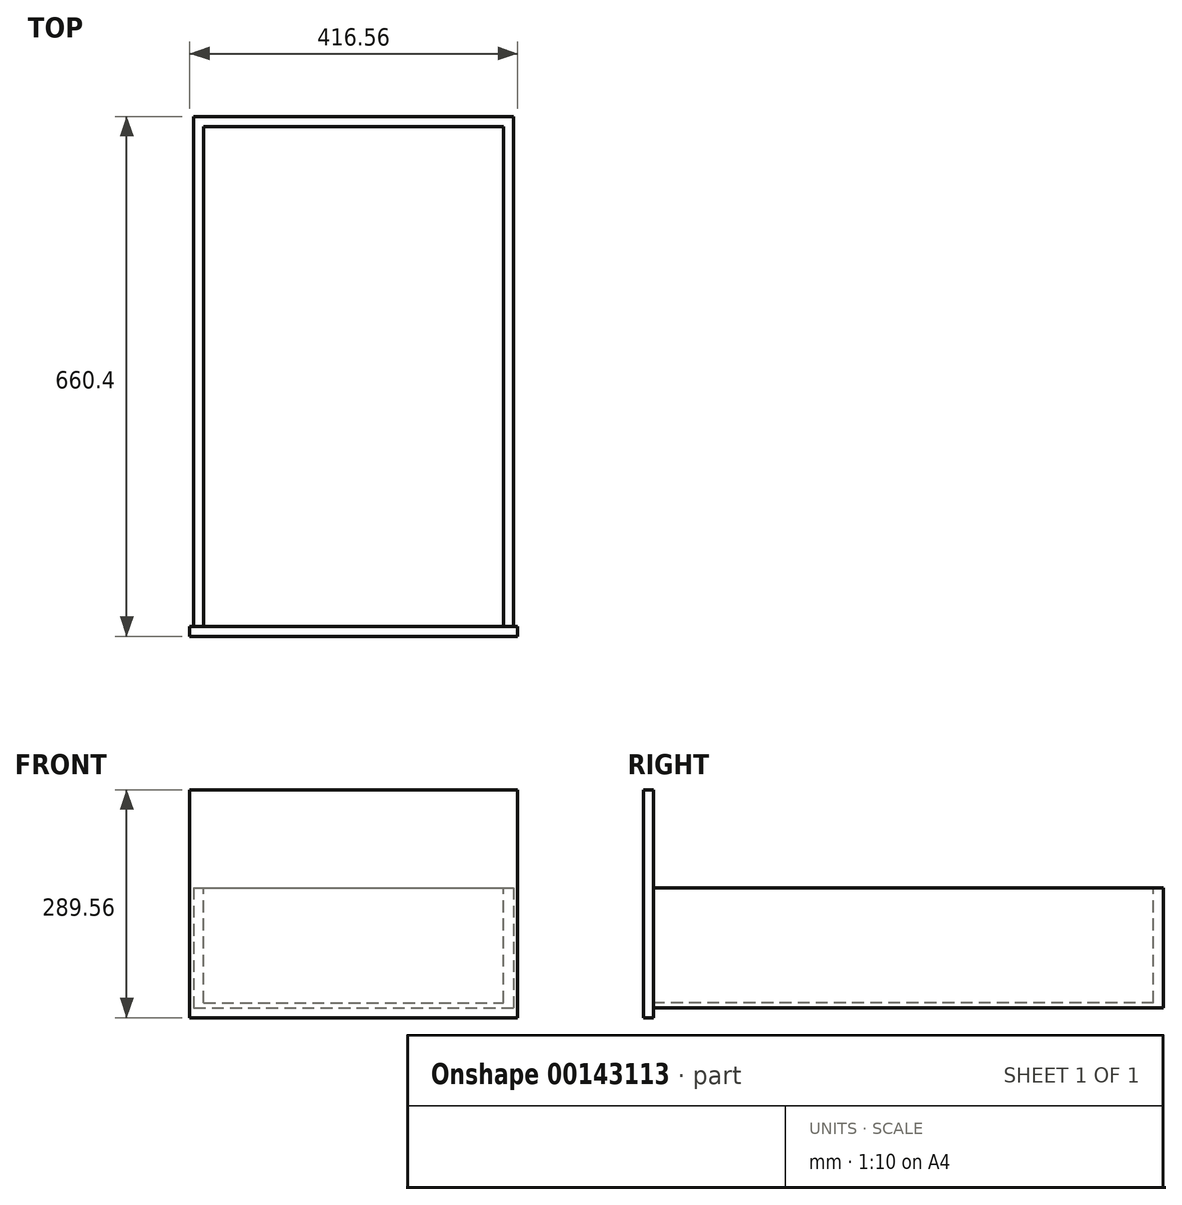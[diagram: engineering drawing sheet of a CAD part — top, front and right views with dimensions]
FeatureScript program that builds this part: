
annotation { "Feature Type Name" : "Feature", "Feature Type Description" : "" }
export const myFeature = defineFeature(function(context is Context, id is Id, definition is map)
    precondition{}
    {
        {
            var Q0;
            Q0=qCreatedBy(makeId("Top.planeOp"),FACE);
            var sketch = newSketch(context, id + "F0", { "sketchPlane" : qUnion([Q0])});
            skLineSegment(sketch, "E0.bottom", {"start": v(0, 0) * mm, "end": v(406.4, 0) * mm});
            skLineSegment(sketch, "E0.top", {"start": v(0, -647.7) * mm, "end": v(406.4, -647.7) * mm});
            skLineSegment(sketch, "E0.left", {"start": v(0, 0) * mm, "end": v(0, -647.7) * mm});
            skLineSegment(sketch, "E0.right", {"start": v(406.4, 0) * mm, "end": v(406.4, -647.7) * mm});
            skSolve(sketch);
        }
        {
            var Q0;
            Q0=makeQuery(id+"F0.imprint","IMPRINT",FACE,{"disambiguationData":[TD([[makeQuery(id+"F0.imprint","IMPRINT",EDGE,{"derivedFrom":sQuery(id+"F0.wireOp",EDGE,"E0.bottom")}),-1.0]])]});
            extrude(context, id + "F1", {"entities" : qUnion([Q0]), "depth" : 152.4 * mm});
        }
        {
            var Q0;
            Q0=makeQuery(id+"F1.opExtrude","SWEPT_FACE",FACE,{"disambiguationData":[OSD([sQuery(id+"F0.wireOp",EDGE,"E0.top")])]});
            var sketch = newSketch(context, id + "F2", { "sketchPlane" : qUnion([Q0])});
            skLineSegment(sketch, "E1.bottom", {"start": v(-5.08, -12.7) * mm, "end": v(411.48, -12.7) * mm});
            skLineSegment(sketch, "E1.top", {"start": v(-5.08, 276.86) * mm, "end": v(411.48, 276.86) * mm});
            skLineSegment(sketch, "E1.left", {"start": v(-5.08, -12.7) * mm, "end": v(-5.08, 276.86) * mm});
            skLineSegment(sketch, "E1.right", {"start": v(411.48, -12.7) * mm, "end": v(411.48, 276.86) * mm});
            skSolve(sketch);
        }
        {
            var Q0;
            Q0=makeQuery(id+"F2.imprint","IMPRINT",FACE,{"disambiguationData":[TD([[makeQuery(id+"F2.imprint","IMPRINT",EDGE,{"derivedFrom":sQuery(id+"F2.wireOp",EDGE,"E1.bottom")}),1.0]])]});
            var Q1;
            {var subQ0=sQuery(id+"F0.wireOp",EDGE,"E0.top");Q1=makeQuery(id+"F2.imprint","IMPRINT",FACE,{"disambiguationData":[TD([[makeQuery(id+"F2.imprint","IMPRINT",EDGE,{"derivedFrom":makeQuery(id+"F1.opExtrude","CAP_EDGE",EDGE,{"disambiguationData":[OSD([subQ0])],"isStart":true})}),1.0]])]});}
            extrude(context, id + "F3", {"entities" : qUnion([Q0, Q1]), "operationType" : NewBodyOperationType.ADD, "depth" : 12.7 * mm});
        }
        {
            var Q0;
            Q0=makeQuery(id+"F1.opExtrude","CAP_FACE",FACE,{"disambiguationData":[OSD([sQuery(id+"F0.wireOp",EDGE,"E0.bottom"),sQuery(id+"F0.wireOp",EDGE,"E0.top"),sQuery(id+"F0.wireOp",EDGE,"E0.left"),sQuery(id+"F0.wireOp",EDGE,"E0.right")])],"isStart":false});
            var sketch = newSketch(context, id + "F4", { "sketchPlane" : qUnion([Q0])});
            skLineSegment(sketch, "E2.bottom", {"start": v(12.7, -12.7) * mm, "end": v(393.7, -12.7) * mm});
            skLineSegment(sketch, "E2.top", {"start": v(12.7, -647.7) * mm, "end": v(393.7, -647.7) * mm});
            skLineSegment(sketch, "E2.left", {"start": v(12.7, -12.7) * mm, "end": v(12.7, -647.7) * mm});
            skLineSegment(sketch, "E2.right", {"start": v(393.7, -12.7) * mm, "end": v(393.7, -647.7) * mm});
            skSolve(sketch);
        }
        {
            var Q0;
            Q0=makeQuery(id+"F4.imprint","IMPRINT",FACE,{"disambiguationData":[TD([[makeQuery(id+"F4.imprint","IMPRINT",EDGE,{"derivedFrom":sQuery(id+"F4.wireOp",EDGE,"E2.bottom")}),-1.0]])]});
            extrude(context, id + "F5", {"entities" : qUnion([Q0]), "operationType" : NewBodyOperationType.REMOVE, "oppositeDirection" : true, "depth" : 146.05 * mm});
        }
    });
